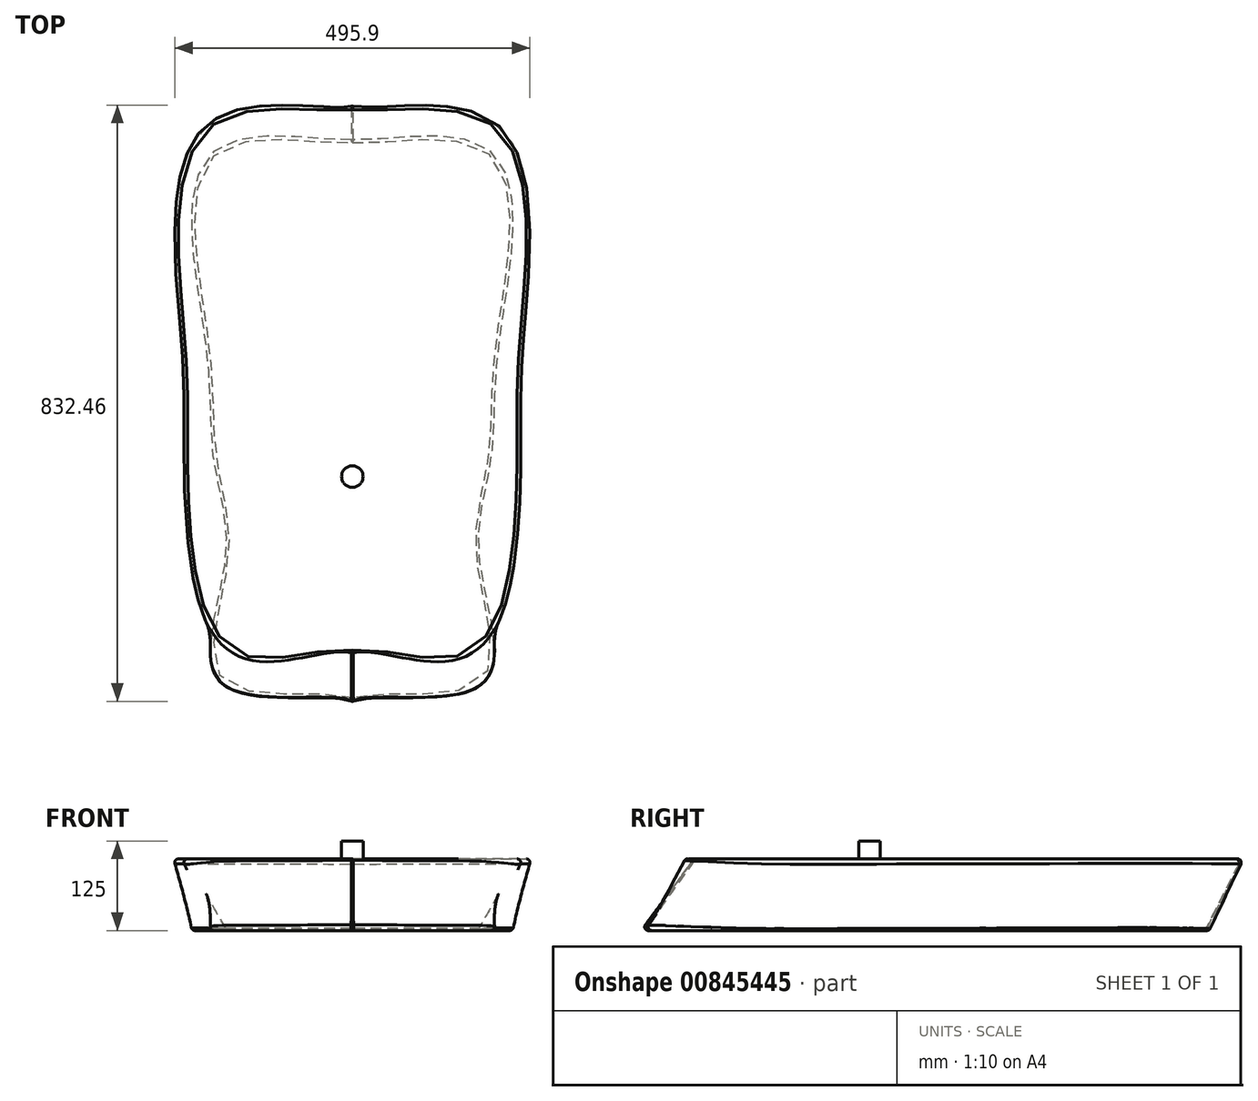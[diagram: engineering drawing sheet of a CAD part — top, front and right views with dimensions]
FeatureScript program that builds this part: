
annotation { "Feature Type Name" : "Feature", "Feature Type Description" : "" }
export const myFeature = defineFeature(function(context is Context, id is Id, definition is map)
    precondition{}
    {
        {
            var Q0;
            Q0=qCreatedBy(makeId("Top.planeOp"),FACE);
            var sketch = newSketch(context, id + "F0", { "sketchPlane" : qUnion([Q0])});
            skFitSpline(sketch, "E0", {"points": [v(0, -300.6) * mm, v(-181.73, -274.67) * mm, v(-176.02, -97.34) * mm, v(-192.13, 39.1) * mm, v(-203.46, 202.92) * mm, v(-187.12, 475.9) * mm, v(0, 488.12) * mm], "startDerivative": vector(-503.9, 266.68) * mm, "endDerivative": vector(282.37, 153.9) * mm});
            skFitSpline(sketch, "E1.MirrorCS", {"points": [v(0, -300.6) * mm, v(181.73, -274.67) * mm, v(176.02, -97.34) * mm, v(192.13, 39.1) * mm, v(203.46, 202.92) * mm, v(187.12, 475.9) * mm, v(0, 488.12) * mm], "startDerivative": vector(503.9, 266.68) * mm, "endDerivative": vector(-282.37, 153.9) * mm});
            skSolve(sketch);
        }
        {
            var Q0;
            Q0=makeQuery(id+"F0.imprint","IMPRINT",FACE,{"disambiguationData":[TD([[makeQuery(id+"F0.imprint","IMPRINT",EDGE,{"derivedFrom":sQuery(id+"F0.wireOp",EDGE,"E0")}),-1.0]])]});
            cPlane(context, id + "F1", {"entities" : qUnion([Q0]), "cplaneType" : CPlaneType.OFFSET, "offset" : 100 * mm, "width" : 150 * mm, "height" : 150 * mm});
        }
        {
            var Q0;
            Q0=qCreatedBy(id+"F1.planeOp",FACE);
            var sketch = newSketch(context, id + "F2", { "sketchPlane" : qUnion([Q0])});
            skFitSpline(sketch, "E2", {"points": [v(0, -226.23) * mm, v(-136.62, -237.35) * mm, v(-219.41, -144.59) * mm, v(-237.96, 63.91) * mm, v(-240.79, 208.57) * mm, v(-197.47, 516.8) * mm, v(0, 539.42) * mm], "startDerivative": vector(-560.56, 177) * mm, "endDerivative": vector(370.82, 170.1) * mm});
            skFitSpline(sketch, "E3.MirrorCS", {"points": [v(0, -226.23) * mm, v(136.62, -237.35) * mm, v(219.41, -144.59) * mm, v(237.96, 63.91) * mm, v(240.79, 208.57) * mm, v(197.47, 516.8) * mm, v(0, 539.42) * mm], "startDerivative": vector(560.56, 177) * mm, "endDerivative": vector(-370.82, 170.1) * mm});
            skSolve(sketch);
        }
        {
            var Q0;
            Q0=makeQuery(id+"F0.imprint","IMPRINT",FACE,{"disambiguationData":[TD([[makeQuery(id+"F0.imprint","IMPRINT",EDGE,{"derivedFrom":sQuery(id+"F0.wireOp",EDGE,"E0")}),-1.0]])]});
            var Q1;
            Q1=makeQuery(id+"F2.imprint","IMPRINT",FACE,{"disambiguationData":[TD([[makeQuery(id+"F2.imprint","IMPRINT",EDGE,{"derivedFrom":sQuery(id+"F2.wireOp",EDGE,"E2")}),-1.0]])]});
            loft(context, id + "F3", {"sheetProfilesArray" : [{ "sheetProfileEntities" : qUnion([Q0]) }, { "sheetProfileEntities" : qUnion([Q1]) }]});
        }
        {
            var Q0;
            {var subQ0=sQuery(id+"F0.wireOp",EDGE,"E1.MirrorCS");var subQ1=sQuery(id+"F0.wireOp",EDGE,"E0");Q0=makeQuery(id+"F3.opLoft","MID_CAP_EDGE",EDGE,{"disambiguationData":[OSD([subQ1,subQ0]),TDD([makeQuery(id+"F0.imprint","INTERSECT",VERTEX,{"disambiguationData":[OD(0.0)],"derivedFrom":[subQ1,subQ0]}),makeQuery(id+"F0.imprint","INTERSECT",VERTEX,{"disambiguationData":[OD(1.0)],"derivedFrom":[subQ1,subQ0]}),makeQuery(id+"F0.imprint","IMPRINT",EDGE,{"derivedFrom":subQ0})])],"capPos":0.0});}
            var Q1;
            {var subQ0=sQuery(id+"F0.wireOp",EDGE,"E0");var subQ1=sQuery(id+"F0.wireOp",EDGE,"E1.MirrorCS");Q1=makeQuery(id+"F3.opLoft","MID_CAP_EDGE",EDGE,{"disambiguationData":[OSD([subQ0,subQ1]),TDD([makeQuery(id+"F0.imprint","INTERSECT",VERTEX,{"disambiguationData":[OD(0.0)],"derivedFrom":[subQ0,subQ1]}),makeQuery(id+"F0.imprint","INTERSECT",VERTEX,{"disambiguationData":[OD(1.0)],"derivedFrom":[subQ0,subQ1]}),makeQuery(id+"F0.imprint","IMPRINT",EDGE,{"derivedFrom":subQ0})])],"capPos":0.0});}
            var Q2;
            {var subQ0=sQuery(id+"F2.wireOp",EDGE,"E3.MirrorCS");var subQ1=sQuery(id+"F2.wireOp",EDGE,"E2");Q2=makeQuery(id+"F3.opLoft","MID_CAP_EDGE",EDGE,{"disambiguationData":[OSD([subQ1,subQ0]),TDD([makeQuery(id+"F2.imprint","INTERSECT",VERTEX,{"disambiguationData":[OD(0.0)],"derivedFrom":[subQ1,subQ0]}),makeQuery(id+"F2.imprint","INTERSECT",VERTEX,{"disambiguationData":[OD(1.0)],"derivedFrom":[subQ1,subQ0]}),makeQuery(id+"F2.imprint","IMPRINT",EDGE,{"derivedFrom":subQ0})])],"capPos":1.0});}
            var Q3;
            {var subQ0=sQuery(id+"F2.wireOp",EDGE,"E2");var subQ1=sQuery(id+"F2.wireOp",EDGE,"E3.MirrorCS");Q3=makeQuery(id+"F3.opLoft","MID_CAP_EDGE",EDGE,{"disambiguationData":[OSD([subQ0,subQ1]),TDD([makeQuery(id+"F2.imprint","INTERSECT",VERTEX,{"disambiguationData":[OD(0.0)],"derivedFrom":[subQ0,subQ1]}),makeQuery(id+"F2.imprint","INTERSECT",VERTEX,{"disambiguationData":[OD(1.0)],"derivedFrom":[subQ0,subQ1]}),makeQuery(id+"F2.imprint","IMPRINT",EDGE,{"derivedFrom":subQ0})])],"capPos":1.0});}
            var Q4;
            {var subQ0=sQuery(id+"F2.wireOp",EDGE,"E3.MirrorCS");var subQ1=sQuery(id+"F2.wireOp",EDGE,"E2");var subQ2=sQuery(id+"F0.wireOp",EDGE,"E1.MirrorCS");var subQ3=sQuery(id+"F0.wireOp",EDGE,"E0");Q4=makeQuery(id+"F3.opLoft","SWEPT_EDGE",EDGE,{"disambiguationData":[OSD([subQ3,subQ2,subQ1,subQ0]),TDD([makeQuery(id+"F0.imprint","INTERSECT",VERTEX,{"disambiguationData":[OD(0.0)],"derivedFrom":[subQ3,subQ2]}),makeQuery(id+"F2.imprint","INTERSECT",VERTEX,{"disambiguationData":[OD(0.0)],"derivedFrom":[subQ1,subQ0]})])]});}
            var Q5;
            {var subQ0=sQuery(id+"F2.wireOp",EDGE,"E3.MirrorCS");var subQ1=sQuery(id+"F2.wireOp",EDGE,"E2");var subQ2=sQuery(id+"F0.wireOp",EDGE,"E1.MirrorCS");var subQ3=sQuery(id+"F0.wireOp",EDGE,"E0");Q5=makeQuery(id+"F3.opLoft","SWEPT_EDGE",EDGE,{"disambiguationData":[OSD([subQ3,subQ2,subQ1,subQ0]),TDD([makeQuery(id+"F0.imprint","INTERSECT",VERTEX,{"disambiguationData":[OD(1.0)],"derivedFrom":[subQ3,subQ2]}),makeQuery(id+"F2.imprint","INTERSECT",VERTEX,{"disambiguationData":[OD(1.0)],"derivedFrom":[subQ1,subQ0]})])]});}
            fillet(context, id + "F4", {"entities" : qUnion([Q0, Q1, Q2, Q3, Q4, Q5]), "radius" : 5 * mm, "tangentPropagation" : true, "allowEdgeOverflow" : false});
        }
        {
            var Q0;
            Q0=makeQuery(id+"F3.opLoft","CAP_FACE",FACE,{"disambiguationData":[OSD([makeQuery(id+"F2.imprint","IMPRINT",FACE,{"disambiguationData":[TD([[makeQuery(id+"F2.imprint","IMPRINT",EDGE,{"derivedFrom":sQuery(id+"F2.wireOp",EDGE,"E2")}),-1.0]])]})])],"isStart":true});
            var sketch = newSketch(context, id + "F5", { "sketchPlane" : qUnion([Q0])});
            skCircle(sketch, "E4", {"center": v(0, 18.63) * mm, "radius": 15 * mm});
            skSolve(sketch);
        }
        {
            var Q0;
            Q0 = qSketchRegion(id + "F5", true);
            extrude(context, id + "F6", {"entities" : qUnion([Q0]), "operationType" : NewBodyOperationType.ADD, "depth" : 25 * mm, "offsetDistance" : 25 * mm});
        }
    });
